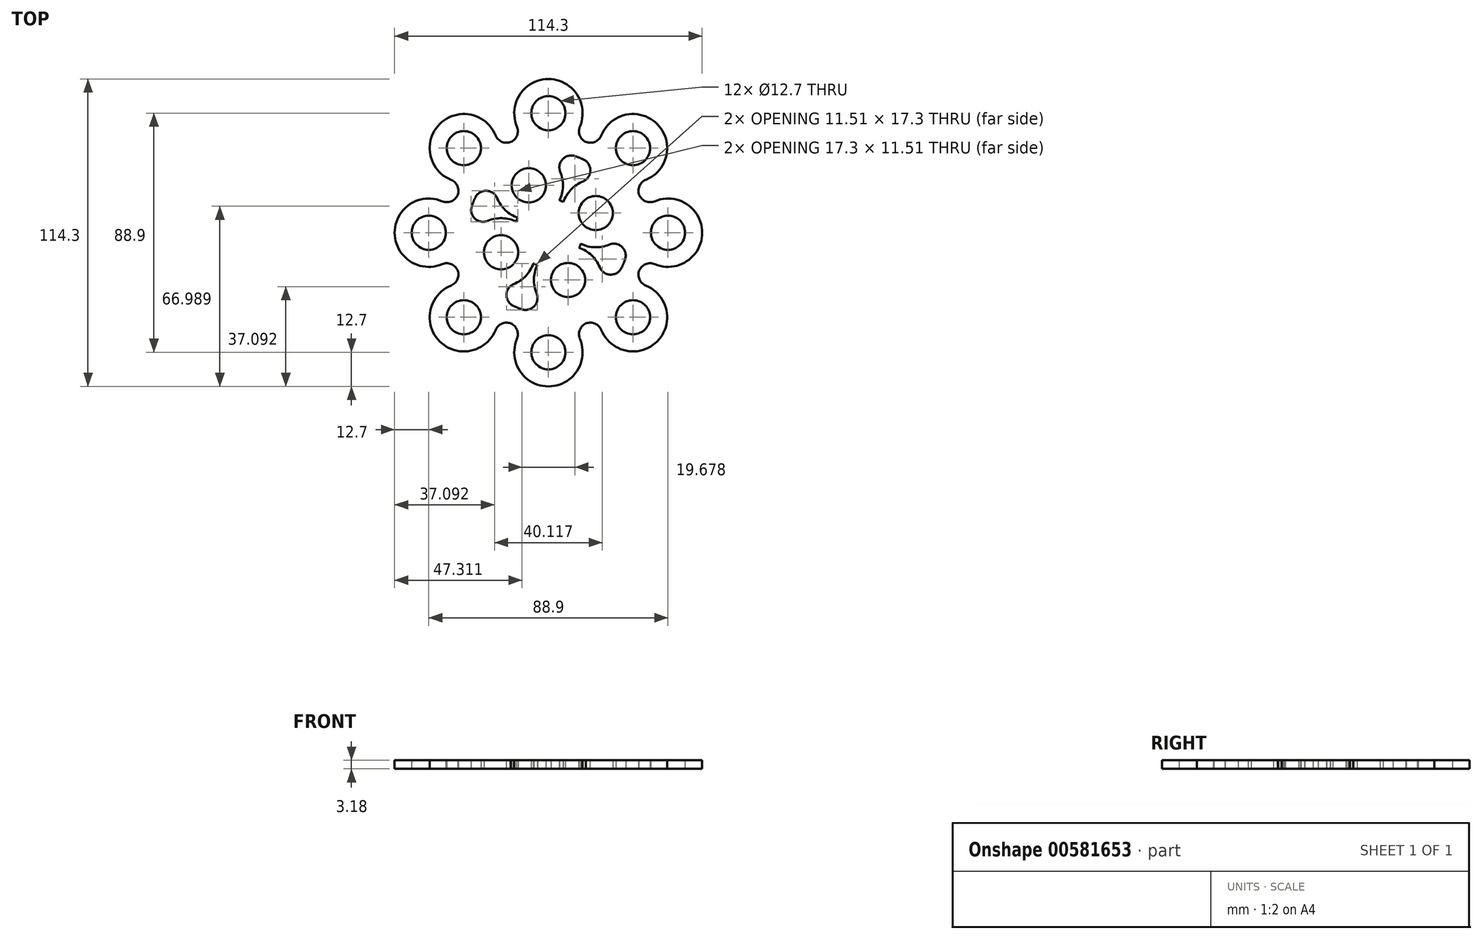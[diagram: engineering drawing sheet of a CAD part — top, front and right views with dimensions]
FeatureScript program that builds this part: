
annotation { "Feature Type Name" : "Feature", "Feature Type Description" : "" }
export const myFeature = defineFeature(function(context is Context, id is Id, definition is map)
    precondition{}
    {
        {
            var Q0;
            Q0=qCreatedBy(makeId("Top.planeOp"),FACE);
            var sketch = newSketch(context, id + "F0", { "sketchPlane" : qUnion([Q0])});
            skCircle(sketch, "E0", {"center": v(0, 0) * mm, "radius": 44.45 * mm, "construction": true});
            skCircle(sketch, "E1.2.0", {"center": v(44.45, 0) * mm, "radius": 6.35 * mm});
            skCircle(sketch, "E1.2.1", {"center": v(44.45, 0) * mm, "radius": 12.7 * mm});
            skCircle(sketch, "E2.1.0", {"center": v(31.43, 31.43) * mm, "radius": 12.7 * mm});
            skCircle(sketch, "E2.1.1", {"center": v(31.43, 31.43) * mm, "radius": 6.35 * mm});
            skCircle(sketch, "E2.2.0", {"center": v(0, 44.45) * mm, "radius": 12.7 * mm});
            skCircle(sketch, "E2.2.1", {"center": v(0, 44.45) * mm, "radius": 6.35 * mm});
            skCircle(sketch, "E3.1.3.0", {"center": v(-31.43, 31.43) * mm, "radius": 12.7 * mm});
            skCircle(sketch, "E3.2.3.0", {"center": v(-31.43, 31.43) * mm, "radius": 6.35 * mm});
            skCircle(sketch, "E3.1.4.0", {"center": v(-44.45, 0) * mm, "radius": 12.7 * mm});
            skCircle(sketch, "E3.2.4.0", {"center": v(-44.45, 0) * mm, "radius": 6.35 * mm});
            skCircle(sketch, "E3.1.5.0", {"center": v(-31.43, -31.43) * mm, "radius": 12.7 * mm});
            skCircle(sketch, "E3.2.5.0", {"center": v(-31.43, -31.43) * mm, "radius": 6.35 * mm});
            skCircle(sketch, "E3.1.6.0", {"center": v(0, -44.45) * mm, "radius": 12.7 * mm});
            skCircle(sketch, "E3.2.6.0", {"center": v(0, -44.45) * mm, "radius": 6.35 * mm});
            skCircle(sketch, "E3.1.7.0", {"center": v(31.43, -31.43) * mm, "radius": 12.7 * mm});
            skCircle(sketch, "E3.2.7.0", {"center": v(31.43, -31.43) * mm, "radius": 6.35 * mm});
            skSolve(sketch);
        }
        {
            var Q0;
            Q0=makeQuery(id+"F0.imprint","IMPRINT",FACE,{"disambiguationData":[TD([[makeQuery(id+"F0.imprint","IMPRINT",EDGE,{"derivedFrom":sQuery(id+"F0.wireOp",EDGE,"E1.2.0")}),-1.0]])]});
            var Q1;
            Q1=makeQuery(id+"F0.imprint","IMPRINT",FACE,{"disambiguationData":[TD([[makeQuery(id+"F0.imprint","IMPRINT",EDGE,{"derivedFrom":sQuery(id+"F0.wireOp",EDGE,"E3.1.7.0")}),1.0]])]});
            var Q2;
            Q2=makeQuery(id+"F0.imprint","IMPRINT",FACE,{"disambiguationData":[TD([[makeQuery(id+"F0.imprint","IMPRINT",EDGE,{"derivedFrom":sQuery(id+"F0.wireOp",EDGE,"E3.1.6.0")}),1.0]])]});
            var Q3;
            Q3=makeQuery(id+"F0.imprint","IMPRINT",FACE,{"disambiguationData":[TD([[makeQuery(id+"F0.imprint","IMPRINT",EDGE,{"derivedFrom":sQuery(id+"F0.wireOp",EDGE,"E3.1.5.0")}),1.0]])]});
            var Q4;
            Q4=makeQuery(id+"F0.imprint","IMPRINT",FACE,{"disambiguationData":[TD([[makeQuery(id+"F0.imprint","IMPRINT",EDGE,{"derivedFrom":sQuery(id+"F0.wireOp",EDGE,"E3.1.4.0")}),1.0]])]});
            var Q5;
            Q5=makeQuery(id+"F0.imprint","IMPRINT",FACE,{"disambiguationData":[TD([[makeQuery(id+"F0.imprint","IMPRINT",EDGE,{"derivedFrom":sQuery(id+"F0.wireOp",EDGE,"E3.1.3.0")}),1.0]])]});
            var Q6;
            Q6=makeQuery(id+"F0.imprint","IMPRINT",FACE,{"disambiguationData":[TD([[makeQuery(id+"F0.imprint","IMPRINT",EDGE,{"derivedFrom":sQuery(id+"F0.wireOp",EDGE,"E2.2.0")}),1.0]])]});
            var Q7;
            Q7=makeQuery(id+"F0.imprint","IMPRINT",FACE,{"disambiguationData":[TD([[makeQuery(id+"F0.imprint","IMPRINT",EDGE,{"derivedFrom":sQuery(id+"F0.wireOp",EDGE,"E2.1.0")}),1.0]])]});
            extrude(context, id + "F1", {"entities" : qUnion([Q0, Q1, Q2, Q3, Q4, Q5, Q6, Q7]), "depth" : 3.17 * mm, "offsetDistance" : 25.4 * mm});
        }
        {
            var Q0;
            Q0=qCreatedBy(makeId("Top.planeOp"),FACE);
            var sketch = newSketch(context, id + "F2", { "sketchPlane" : qUnion([Q0])});
            skCircle(sketch, "E4", {"center": v(0, 0) * mm, "radius": 30.16 * mm});
            skCircle(sketch, "E5", {"center": v(0, 0) * mm, "radius": 36.51 * mm});
            skSolve(sketch);
        }
        {
            var Q0;
            Q0 = qSketchRegion(id + "F2", true);
            extrude(context, id + "F3", {"entities" : qUnion([Q0]), "operationType" : NewBodyOperationType.ADD, "depth" : 3.17 * mm, "offsetDistance" : 25.4 * mm});
        }
        {
            var Q0;
            Q0=makeQuery(id+"F3.boolean.opBoolean","INTERSECT",EDGE,{"disambiguationData":[OD(1.0)],"derivedFrom":[makeQuery(id+"F1.opExtrude","SWEPT_FACE",FACE,{"disambiguationData":[OSD([sQuery(id+"F0.wireOp",EDGE,"E3.1.7.0")])]}),makeQuery(id+"F3.opExtrude","SWEPT_FACE",FACE,{"disambiguationData":[OSD([sQuery(id+"F2.wireOp",EDGE,"E5")])]})]});
            var Q1;
            Q1=makeQuery(id+"F3.boolean.opBoolean","INTERSECT",EDGE,{"disambiguationData":[OD(1.0)],"derivedFrom":[makeQuery(id+"F1.opExtrude","SWEPT_FACE",FACE,{"disambiguationData":[OSD([sQuery(id+"F0.wireOp",EDGE,"E3.1.6.0")])]}),makeQuery(id+"F3.opExtrude","SWEPT_FACE",FACE,{"disambiguationData":[OSD([sQuery(id+"F2.wireOp",EDGE,"E5")])]})]});
            var Q2;
            Q2=makeQuery(id+"F3.boolean.opBoolean","INTERSECT",EDGE,{"disambiguationData":[OD(1.0)],"derivedFrom":[makeQuery(id+"F1.opExtrude","SWEPT_FACE",FACE,{"disambiguationData":[OSD([sQuery(id+"F0.wireOp",EDGE,"E1.2.1")])]}),makeQuery(id+"F3.opExtrude","SWEPT_FACE",FACE,{"disambiguationData":[OSD([sQuery(id+"F2.wireOp",EDGE,"E5")])]})]});
            var Q3;
            Q3=makeQuery(id+"F3.boolean.opBoolean","INTERSECT",EDGE,{"disambiguationData":[OD(0.0)],"derivedFrom":[makeQuery(id+"F1.opExtrude","SWEPT_FACE",FACE,{"disambiguationData":[OSD([sQuery(id+"F0.wireOp",EDGE,"E3.1.7.0")])]}),makeQuery(id+"F3.opExtrude","SWEPT_FACE",FACE,{"disambiguationData":[OSD([sQuery(id+"F2.wireOp",EDGE,"E5")])]})]});
            var Q4;
            Q4=makeQuery(id+"F3.boolean.opBoolean","INTERSECT",EDGE,{"disambiguationData":[OD(0.0)],"derivedFrom":[makeQuery(id+"F1.opExtrude","SWEPT_FACE",FACE,{"disambiguationData":[OSD([sQuery(id+"F0.wireOp",EDGE,"E1.2.1")])]}),makeQuery(id+"F3.opExtrude","SWEPT_FACE",FACE,{"disambiguationData":[OSD([sQuery(id+"F2.wireOp",EDGE,"E5")])]})]});
            var Q5;
            Q5=makeQuery(id+"F3.boolean.opBoolean","INTERSECT",EDGE,{"disambiguationData":[OD(0.0)],"derivedFrom":[makeQuery(id+"F1.opExtrude","SWEPT_FACE",FACE,{"disambiguationData":[OSD([sQuery(id+"F0.wireOp",EDGE,"E2.1.0")])]}),makeQuery(id+"F3.opExtrude","SWEPT_FACE",FACE,{"disambiguationData":[OSD([sQuery(id+"F2.wireOp",EDGE,"E5")])]})]});
            var Q6;
            Q6=makeQuery(id+"F3.boolean.opBoolean","INTERSECT",EDGE,{"disambiguationData":[OD(0.0)],"derivedFrom":[makeQuery(id+"F1.opExtrude","SWEPT_FACE",FACE,{"disambiguationData":[OSD([sQuery(id+"F0.wireOp",EDGE,"E2.2.0")])]}),makeQuery(id+"F3.opExtrude","SWEPT_FACE",FACE,{"disambiguationData":[OSD([sQuery(id+"F2.wireOp",EDGE,"E5")])]})]});
            var Q7;
            Q7=makeQuery(id+"F3.boolean.opBoolean","INTERSECT",EDGE,{"disambiguationData":[OD(1.0)],"derivedFrom":[makeQuery(id+"F1.opExtrude","SWEPT_FACE",FACE,{"disambiguationData":[OSD([sQuery(id+"F0.wireOp",EDGE,"E2.1.0")])]}),makeQuery(id+"F3.opExtrude","SWEPT_FACE",FACE,{"disambiguationData":[OSD([sQuery(id+"F2.wireOp",EDGE,"E5")])]})]});
            var Q8;
            Q8=makeQuery(id+"F3.boolean.opBoolean","INTERSECT",EDGE,{"disambiguationData":[OD(0.0)],"derivedFrom":[makeQuery(id+"F1.opExtrude","SWEPT_FACE",FACE,{"disambiguationData":[OSD([sQuery(id+"F0.wireOp",EDGE,"E3.1.3.0")])]}),makeQuery(id+"F3.opExtrude","SWEPT_FACE",FACE,{"disambiguationData":[OSD([sQuery(id+"F2.wireOp",EDGE,"E5")])]})]});
            var Q9;
            Q9=makeQuery(id+"F3.boolean.opBoolean","INTERSECT",EDGE,{"disambiguationData":[OD(1.0)],"derivedFrom":[makeQuery(id+"F1.opExtrude","SWEPT_FACE",FACE,{"disambiguationData":[OSD([sQuery(id+"F0.wireOp",EDGE,"E2.2.0")])]}),makeQuery(id+"F3.opExtrude","SWEPT_FACE",FACE,{"disambiguationData":[OSD([sQuery(id+"F2.wireOp",EDGE,"E5")])]})]});
            var Q10;
            Q10=makeQuery(id+"F3.boolean.opBoolean","INTERSECT",EDGE,{"disambiguationData":[OD(0.0)],"derivedFrom":[makeQuery(id+"F1.opExtrude","SWEPT_FACE",FACE,{"disambiguationData":[OSD([sQuery(id+"F0.wireOp",EDGE,"E3.1.4.0")])]}),makeQuery(id+"F3.opExtrude","SWEPT_FACE",FACE,{"disambiguationData":[OSD([sQuery(id+"F2.wireOp",EDGE,"E5")])]})]});
            var Q11;
            Q11=makeQuery(id+"F3.boolean.opBoolean","INTERSECT",EDGE,{"disambiguationData":[OD(1.0)],"derivedFrom":[makeQuery(id+"F1.opExtrude","SWEPT_FACE",FACE,{"disambiguationData":[OSD([sQuery(id+"F0.wireOp",EDGE,"E3.1.3.0")])]}),makeQuery(id+"F3.opExtrude","SWEPT_FACE",FACE,{"disambiguationData":[OSD([sQuery(id+"F2.wireOp",EDGE,"E5")])]})]});
            var Q12;
            Q12=makeQuery(id+"F3.boolean.opBoolean","INTERSECT",EDGE,{"disambiguationData":[OD(0.0)],"derivedFrom":[makeQuery(id+"F1.opExtrude","SWEPT_FACE",FACE,{"disambiguationData":[OSD([sQuery(id+"F0.wireOp",EDGE,"E3.1.5.0")])]}),makeQuery(id+"F3.opExtrude","SWEPT_FACE",FACE,{"disambiguationData":[OSD([sQuery(id+"F2.wireOp",EDGE,"E5")])]})]});
            var Q13;
            Q13=makeQuery(id+"F3.boolean.opBoolean","INTERSECT",EDGE,{"disambiguationData":[OD(1.0)],"derivedFrom":[makeQuery(id+"F1.opExtrude","SWEPT_FACE",FACE,{"disambiguationData":[OSD([sQuery(id+"F0.wireOp",EDGE,"E3.1.4.0")])]}),makeQuery(id+"F3.opExtrude","SWEPT_FACE",FACE,{"disambiguationData":[OSD([sQuery(id+"F2.wireOp",EDGE,"E5")])]})]});
            var Q14;
            Q14=makeQuery(id+"F3.boolean.opBoolean","INTERSECT",EDGE,{"disambiguationData":[OD(0.0)],"derivedFrom":[makeQuery(id+"F1.opExtrude","SWEPT_FACE",FACE,{"disambiguationData":[OSD([sQuery(id+"F0.wireOp",EDGE,"E3.1.6.0")])]}),makeQuery(id+"F3.opExtrude","SWEPT_FACE",FACE,{"disambiguationData":[OSD([sQuery(id+"F2.wireOp",EDGE,"E5")])]})]});
            var Q15;
            Q15=makeQuery(id+"F3.boolean.opBoolean","INTERSECT",EDGE,{"disambiguationData":[OD(1.0)],"derivedFrom":[makeQuery(id+"F1.opExtrude","SWEPT_FACE",FACE,{"disambiguationData":[OSD([sQuery(id+"F0.wireOp",EDGE,"E3.1.5.0")])]}),makeQuery(id+"F3.opExtrude","SWEPT_FACE",FACE,{"disambiguationData":[OSD([sQuery(id+"F2.wireOp",EDGE,"E5")])]})]});
            fillet(context, id + "F4", {"entities" : qUnion([Q0, Q1, Q2, Q3, Q4, Q5, Q6, Q7, Q8, Q9, Q10, Q11, Q12, Q13, Q14, Q15]), "radius" : 4.44 * mm, "tangentPropagation" : true, "allowEdgeOverflow" : false});
        }
        {
            var Q0;
            Q0=qCreatedBy(makeId("Top.planeOp"),FACE);
            var sketch = newSketch(context, id + "F5", { "sketchPlane" : qUnion([Q0])});
            skCircle(sketch, "E6", {"center": v(0, 0) * mm, "radius": 19.05 * mm, "construction": true});
            skCircle(sketch, "E7", {"center": v(17.6, 7.3) * mm, "radius": 12.7 * mm});
            skCircle(sketch, "E8", {"center": v(17.6, 7.3) * mm, "radius": 6.35 * mm});
            skLineSegment(sketch, "E9", {"start": v(17.6, 7.3) * mm, "end": v(0, 0) * mm, "construction": true});
            skLineSegment(sketch, "E10", {"start": v(0, 0) * mm, "end": v(19.05, 0) * mm, "construction": true});
            skCircle(sketch, "E11.1.0", {"center": v(-7.3, 17.6) * mm, "radius": 12.7 * mm});
            skCircle(sketch, "E11.1.1", {"center": v(-7.3, 17.6) * mm, "radius": 6.35 * mm});
            skCircle(sketch, "E11.2.0", {"center": v(-17.6, -7.3) * mm, "radius": 12.7 * mm});
            skCircle(sketch, "E11.2.1", {"center": v(-17.6, -7.3) * mm, "radius": 6.35 * mm});
            skCircle(sketch, "E12.1.3.0", {"center": v(7.3, -17.6) * mm, "radius": 12.7 * mm});
            skCircle(sketch, "E12.2.3.0", {"center": v(7.3, -17.6) * mm, "radius": 6.35 * mm});
            skCircle(sketch, "E13", {"center": v(0, 0) * mm, "radius": 12.7 * mm});
            skSolve(sketch);
        }
        {
            var Q0;
            {var subQ4=sQuery(id+"F5.wireOp",EDGE,"E11.1.1");Q0=makeQuery(id+"F5.imprint","IMPRINT",FACE,{"disambiguationData":[TD([[makeQuery(id+"F5.imprint","IMPRINT",EDGE,{"derivedFrom":subQ4}),-1.0]])]});}
            var Q1;
            {var subQ4=sQuery(id+"F5.wireOp",EDGE,"E11.2.1");Q1=makeQuery(id+"F5.imprint","IMPRINT",FACE,{"disambiguationData":[TD([[makeQuery(id+"F5.imprint","IMPRINT",EDGE,{"derivedFrom":subQ4}),-1.0]])]});}
            var Q2;
            {var subQ4=sQuery(id+"F5.wireOp",EDGE,"E12.2.3.0");Q2=makeQuery(id+"F5.imprint","IMPRINT",FACE,{"disambiguationData":[TD([[makeQuery(id+"F5.imprint","IMPRINT",EDGE,{"derivedFrom":subQ4}),-1.0]])]});}
            var Q3;
            {var subQ4=sQuery(id+"F5.wireOp",EDGE,"E8");Q3=makeQuery(id+"F5.imprint","IMPRINT",FACE,{"disambiguationData":[TD([[makeQuery(id+"F5.imprint","IMPRINT",EDGE,{"derivedFrom":subQ4}),-1.0]])]});}
            var Q4;
            {var subQ0=sQuery(id+"F5.wireOp",EDGE,"E13");var subQ10=sQuery(id+"F5.wireOp",EDGE,"E7");var subQ11=makeQuery(id+"F5.imprint","INTERSECT",VERTEX,{"disambiguationData":[OD(0.0)],"derivedFrom":[subQ10,subQ0]});Q4=makeQuery(id+"F5.imprint","IMPRINT",FACE,{"disambiguationData":[TD([[makeQuery(id+"F5.imprint","IMPRINT",EDGE,{"disambiguationData":[TD([[subQ11,-1.0]])],"derivedFrom":subQ10}),-1.0]])]});}
            var Q5;
            {var subQ0=sQuery(id+"F5.wireOp",EDGE,"E13");var subQ1=sQuery(id+"F5.wireOp",EDGE,"E11.2.0");var subQ2=makeQuery(id+"F5.imprint","INTERSECT",VERTEX,{"disambiguationData":[OD(0.0)],"derivedFrom":[subQ1,subQ0]});Q5=makeQuery(id+"F5.imprint","IMPRINT",FACE,{"disambiguationData":[TD([[makeQuery(id+"F5.imprint","IMPRINT",EDGE,{"disambiguationData":[TD([[subQ2,1.0]])],"derivedFrom":subQ1}),1.0]])]});}
            var Q6;
            {var subQ0=sQuery(id+"F5.wireOp",EDGE,"E13");var subQ1=sQuery(id+"F5.wireOp",EDGE,"E11.1.0");var subQ2=makeQuery(id+"F5.imprint","INTERSECT",VERTEX,{"disambiguationData":[OD(0.0)],"derivedFrom":[subQ1,subQ0]});Q6=makeQuery(id+"F5.imprint","IMPRINT",FACE,{"disambiguationData":[TD([[makeQuery(id+"F5.imprint","IMPRINT",EDGE,{"disambiguationData":[TD([[subQ2,1.0]])],"derivedFrom":subQ1}),1.0]])]});}
            var Q7;
            {var subQ0=sQuery(id+"F5.wireOp",EDGE,"E13");var subQ1=sQuery(id+"F5.wireOp",EDGE,"E7");var subQ2=makeQuery(id+"F5.imprint","INTERSECT",VERTEX,{"disambiguationData":[OD(0.0)],"derivedFrom":[subQ1,subQ0]});Q7=makeQuery(id+"F5.imprint","IMPRINT",FACE,{"disambiguationData":[TD([[makeQuery(id+"F5.imprint","IMPRINT",EDGE,{"disambiguationData":[TD([[subQ2,-1.0]])],"derivedFrom":subQ1}),1.0]])]});}
            var Q8;
            {var subQ0=sQuery(id+"F5.wireOp",EDGE,"E13");var subQ1=sQuery(id+"F5.wireOp",EDGE,"E12.1.3.0");var subQ2=makeQuery(id+"F5.imprint","INTERSECT",VERTEX,{"disambiguationData":[OD(0.0)],"derivedFrom":[subQ1,subQ0]});Q8=makeQuery(id+"F5.imprint","IMPRINT",FACE,{"disambiguationData":[TD([[makeQuery(id+"F5.imprint","IMPRINT",EDGE,{"disambiguationData":[TD([[subQ2,1.0]])],"derivedFrom":subQ1}),1.0]])]});}
            extrude(context, id + "F6", {"entities" : qUnion([Q0, Q1, Q2, Q3, Q4, Q5, Q6, Q7, Q8]), "operationType" : NewBodyOperationType.ADD, "depth" : 3.17 * mm, "offsetDistance" : 25.4 * mm});
        }
        {
            var Q0;
            Q0=makeQuery(id+"F6.boolean.opBoolean","INTERSECT",EDGE,{"disambiguationData":[OD(1.0)],"derivedFrom":[makeQuery(id+"F3.opExtrude","SWEPT_FACE",FACE,{"disambiguationData":[OSD([sQuery(id+"F2.wireOp",EDGE,"E4")])]}),makeQuery(id+"F6.opExtrude","SWEPT_FACE",FACE,{"disambiguationData":[OSD([sQuery(id+"F5.wireOp",EDGE,"E11.1.0")])]})]});
            var Q1;
            Q1=makeQuery(id+"F6.boolean.opBoolean","INTERSECT",EDGE,{"disambiguationData":[OD(0.0)],"derivedFrom":[makeQuery(id+"F3.opExtrude","SWEPT_FACE",FACE,{"disambiguationData":[OSD([sQuery(id+"F2.wireOp",EDGE,"E4")])]}),makeQuery(id+"F6.opExtrude","SWEPT_FACE",FACE,{"disambiguationData":[OSD([sQuery(id+"F5.wireOp",EDGE,"E11.2.0")])]})]});
            var Q2;
            Q2=makeQuery(id+"F6.boolean.opBoolean","INTERSECT",EDGE,{"disambiguationData":[OD(0.0)],"derivedFrom":[makeQuery(id+"F3.opExtrude","SWEPT_FACE",FACE,{"disambiguationData":[OSD([sQuery(id+"F2.wireOp",EDGE,"E4")])]}),makeQuery(id+"F6.opExtrude","SWEPT_FACE",FACE,{"disambiguationData":[OSD([sQuery(id+"F5.wireOp",EDGE,"E7")])]})]});
            var Q3;
            Q3=makeQuery(id+"F6.boolean.opBoolean","INTERSECT",EDGE,{"disambiguationData":[OD(0.0)],"derivedFrom":[makeQuery(id+"F3.opExtrude","SWEPT_FACE",FACE,{"disambiguationData":[OSD([sQuery(id+"F2.wireOp",EDGE,"E4")])]}),makeQuery(id+"F6.opExtrude","SWEPT_FACE",FACE,{"disambiguationData":[OSD([sQuery(id+"F5.wireOp",EDGE,"E11.1.0")])]})]});
            var Q4;
            Q4=makeQuery(id+"F6.boolean.opBoolean","INTERSECT",EDGE,{"disambiguationData":[OD(1.0)],"derivedFrom":[makeQuery(id+"F3.opExtrude","SWEPT_FACE",FACE,{"disambiguationData":[OSD([sQuery(id+"F2.wireOp",EDGE,"E4")])]}),makeQuery(id+"F6.opExtrude","SWEPT_FACE",FACE,{"disambiguationData":[OSD([sQuery(id+"F5.wireOp",EDGE,"E12.1.3.0")])]})]});
            var Q5;
            Q5=makeQuery(id+"F6.boolean.opBoolean","INTERSECT",EDGE,{"disambiguationData":[OD(1.0)],"derivedFrom":[makeQuery(id+"F3.opExtrude","SWEPT_FACE",FACE,{"disambiguationData":[OSD([sQuery(id+"F2.wireOp",EDGE,"E4")])]}),makeQuery(id+"F6.opExtrude","SWEPT_FACE",FACE,{"disambiguationData":[OSD([sQuery(id+"F5.wireOp",EDGE,"E7")])]})]});
            var Q6;
            Q6=makeQuery(id+"F6.boolean.opBoolean","INTERSECT",EDGE,{"disambiguationData":[OD(1.0)],"derivedFrom":[makeQuery(id+"F3.opExtrude","SWEPT_FACE",FACE,{"disambiguationData":[OSD([sQuery(id+"F2.wireOp",EDGE,"E4")])]}),makeQuery(id+"F6.opExtrude","SWEPT_FACE",FACE,{"disambiguationData":[OSD([sQuery(id+"F5.wireOp",EDGE,"E11.2.0")])]})]});
            var Q7;
            Q7=makeQuery(id+"F6.boolean.opBoolean","INTERSECT",EDGE,{"disambiguationData":[OD(0.0)],"derivedFrom":[makeQuery(id+"F3.opExtrude","SWEPT_FACE",FACE,{"disambiguationData":[OSD([sQuery(id+"F2.wireOp",EDGE,"E4")])]}),makeQuery(id+"F6.opExtrude","SWEPT_FACE",FACE,{"disambiguationData":[OSD([sQuery(id+"F5.wireOp",EDGE,"E12.1.3.0")])]})]});
            fillet(context, id + "F7", {"entities" : qUnion([Q0, Q1, Q2, Q3, Q4, Q5, Q6, Q7]), "radius" : 4.44 * mm, "tangentPropagation" : true, "allowEdgeOverflow" : false});
        }
    });
